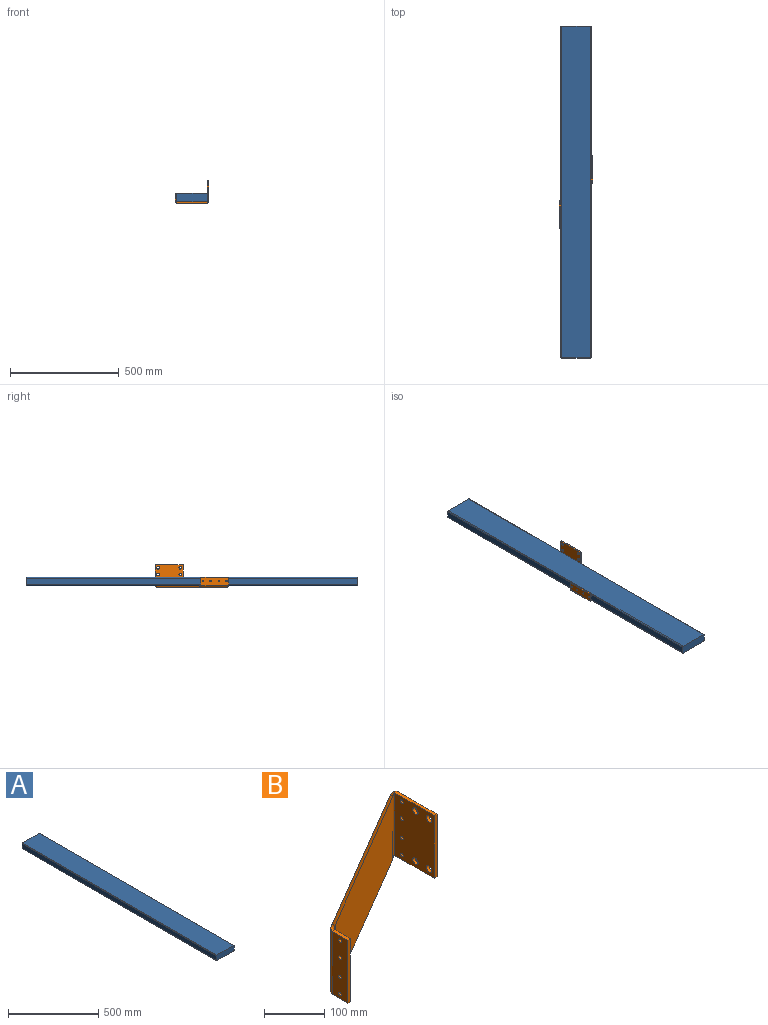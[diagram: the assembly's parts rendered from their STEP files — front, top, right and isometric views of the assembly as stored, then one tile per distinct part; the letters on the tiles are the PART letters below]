
ASSEMBLY  parts=2 mates=1
PART A: 10 faces, bbox 139.7x1524x38.1 mm
  f0: plane 1524x30.48mm, normal (-1,0,0), area 46451.5mm2, adj f4,f5,f6,f9
  f1: plane 1524x132.08mm, normal (0,0,-1), area 201289.9mm2, adj f4,f5,f6,f7
  f2: plane 1524x30.48mm, normal (1,0,0), area 46451.5mm2, adj f4,f5,f7,f8
  f3: plane 1524x132.08mm, normal (0,0,1), area 201289.9mm2, adj f4,f5,f8,f9
  f4: plane 139.7x38.1mm, normal (0,-1,0), area 5310.1mm2, adj f0,f1,f2,f3,f6,f7,f8,f9
  f5: plane 139.7x38.1mm, normal (0,1,0), area 5310.1mm2, adj f0,f1,f2,f3,f6,f7,f8,f9
  f6: cylinder r=3.81mm len=1524mm, axis (0,1,0), area 9120.7mm2, adj f0,f1,f4,f5
  f7: cylinder r=3.81mm len=1524mm, axis (0,-1,0), area 9120.7mm2, adj f1,f2,f4,f5
  f8: cylinder r=3.81mm len=1524mm, axis (0,1,0), area 9120.7mm2, adj f2,f3,f4,f5
  f9: cylinder r=3.81mm len=1524mm, axis (0,-1,0), area 9120.7mm2, adj f0,f3,f4,f5
PART B: 34 faces, bbox 152.4x101.6x335.6 mm
  f0: plane 192.98x135.13mm, normal (0.82,0,-0.57), area 1496mm2, adj f2,f3,f14,f30
  f1: plane 192.98x135.13mm, normal (-0.82,0,0.57), area 1496mm2, adj f2,f3,f13,f31
  f2: plane 319.98x135.13mm, normal (0,1,0), area 17161.3mm2, adj f0,f1,f15,f32
  f3: plane 319.98x135.13mm, normal (0,-1,0), area 17161.3mm2, adj f0,f1,f16,f33
  f4: plane 35.81x6.35mm, normal (0,0,1), area 227.4mm2, adj f10,f11,f12,f13
  f5: plane 35.81x6.35mm, normal (0,0,-1), area 227.4mm2, adj f10,f11,f12,f14
  f6: cylinder r=3.17mm len=6.35mm, axis (-1,0,0), area 126.7mm2, adj f11,f12
  f7: cylinder r=3.17mm len=6.35mm, axis (-1,0,0), area 126.7mm2, adj f11,f12
  f8: cylinder r=3.17mm len=6.35mm, axis (-1,0,0), area 126.7mm2, adj f11,f12
  f9: cylinder r=3.17mm len=6.35mm, axis (-1,0,0), area 126.7mm2, adj f11,f12
  f10: plane 127x6.35mm, normal (0,-1,0), area 806.5mm2, adj f4,f5,f11,f12
  f11: plane 127x35.81mm, normal (-1,0,0), area 4421.7mm2, adj f4,f5,f6,f7,f8,f9,f10,f15
  f12: plane 127x35.81mm, normal (1,0,0), area 4421.7mm2, adj f4,f5,f6,f7,f8,f9,f10,f16
  f13: bspline ~8.64x8.64mm, area 78.9mm2, adj f1,f4,f15,f16
  f14: bspline ~8.64x8.64mm, area 76.5mm2, adj f0,f5,f15,f16
  f15: cylinder r=8.64mm len=134.8mm, axis (0,0,1), area 1715.3mm2, adj f2,f11,f13,f14
  f16: cylinder r=2.29mm len=134.8mm, axis (0,0,1), area 454mm2, adj f3,f12,f13,f14
  f17: plane 92.96x6.35mm, normal (0,0,-1), area 590.3mm2, adj f27,f28,f29,f30
  f18: plane 92.96x6.35mm, normal (0,0,1), area 590.3mm2, adj f27,f28,f29,f31
  f19: cylinder r=3.17mm len=6.35mm, axis (1,0,0), area 126.7mm2, adj f28,f29
  f20: cylinder r=3.17mm len=6.35mm, axis (1,0,0), area 126.7mm2, adj f28,f29
  f21: cylinder r=3.17mm len=6.35mm, axis (1,0,0), area 126.7mm2, adj f28,f29
  f22: cylinder r=3.17mm len=6.35mm, axis (1,0,0), area 126.7mm2, adj f28,f29
  f23: cylinder r=6.35mm len=12.7mm, axis (1,0,0), area 253.4mm2, adj f28,f29
  f24: cylinder r=6.35mm len=12.7mm, axis (1,0,0), area 253.4mm2, adj f28,f29
  f25: cylinder r=6.35mm len=12.7mm, axis (1,0,0), area 253.4mm2, adj f28,f29
  f26: cylinder r=6.35mm len=12.7mm, axis (1,0,0), area 253.4mm2, adj f28,f29
  f27: plane 127x6.35mm, normal (0,-1,0), area 806.5mm2, adj f17,f18,f28,f29
  f28: plane 127x92.96mm, normal (1,0,0), area 11173mm2, adj f17,f18,f19,f20,f21,f22,f23,f24
  f29: plane 127x92.96mm, normal (-1,0,0), area 11173mm2, adj f17,f18,f19,f20,f21,f22,f23,f24
  f30: bspline ~8.64x8.64mm, area 78.9mm2, adj f0,f17,f32,f33
  f31: bspline ~8.64x8.64mm, area 76.5mm2, adj f1,f18,f32,f33
  f32: cylinder r=8.64mm len=134.8mm, axis (0,0,-1), area 1715.3mm2, adj f2,f28,f30,f31
  f33: cylinder r=2.29mm len=134.8mm, axis (0,0,-1), area 454mm2, adj f3,f29,f30,f31
PLACE A t=(-269.41,420.4,-279.09)mm
PLACE B rot(axis=(-1,0,0),90deg) t=(-269.41,-305.34,-304.49)mm
MATE parallel B.f3 <-> A.f1  axis (0,0,1) through (-269.41,-341.6,-298.14)mm
